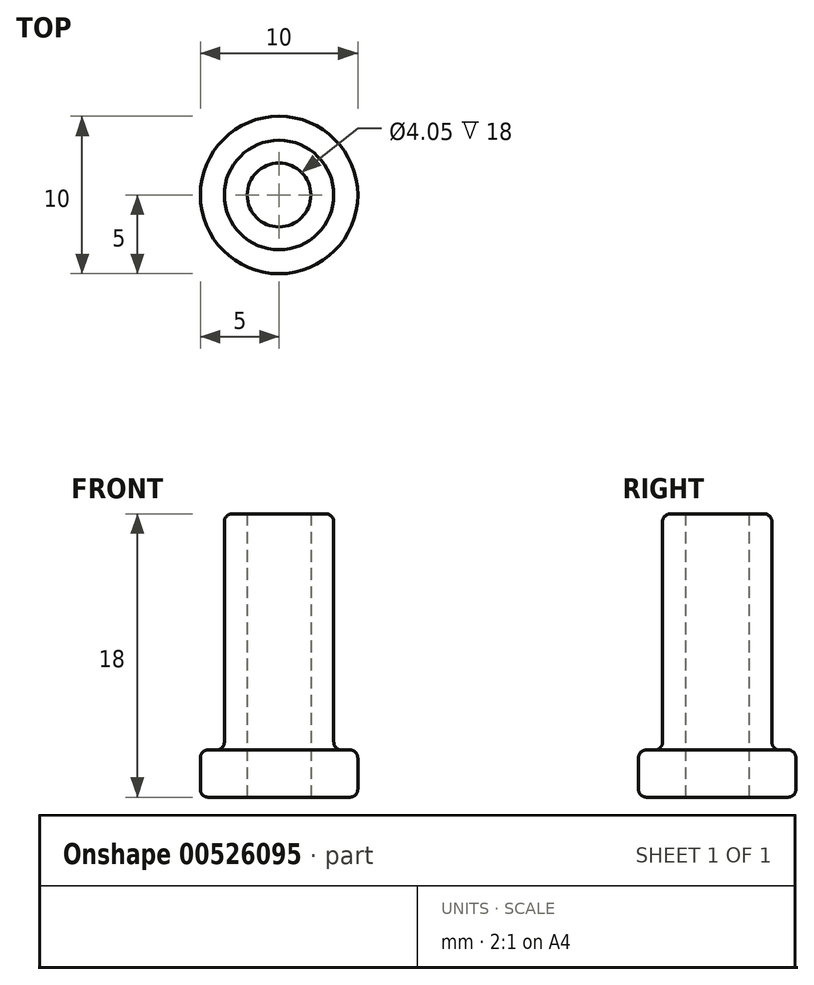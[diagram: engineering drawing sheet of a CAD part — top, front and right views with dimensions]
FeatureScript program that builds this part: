
annotation { "Feature Type Name" : "Feature", "Feature Type Description" : "" }
export const myFeature = defineFeature(function(context is Context, id is Id, definition is map)
    precondition{}
    {
        {
            var Q0;
            Q0=qCreatedBy(makeId("Front.planeOp"),FACE);
            var sketch = newSketch(context, id + "F0", { "sketchPlane" : qUnion([Q0])});
            skLineSegment(sketch, "E0", {"start": v(0, 0) * mm, "end": v(0, 40) * mm});
            skLineSegment(sketch, "E1", {"start": v(2.02, 0) * mm, "end": v(5, 0) * mm});
            skLineSegment(sketch, "E2.0", {"start": v(2.02, 18) * mm, "end": v(3.47, 18) * mm});
            skLineSegment(sketch, "E3.0", {"start": v(3.47, 3) * mm, "end": v(5, 3) * mm});
            skLineSegment(sketch, "E4.0", {"start": v(5, 0) * mm, "end": v(5, 3) * mm});
            skPoint(sketch, "E5.orphan", {"position": v(-20.83, 0) * mm});
            skLineSegment(sketch, "E6.0", {"start": v(2.02, 0) * mm, "end": v(2.02, 18) * mm});
            skLineSegment(sketch, "E7", {"start": v(3.47, 18) * mm, "end": v(3.47, 3) * mm});
            skSolve(sketch);
        }
        {
            var Q0;
            Q0=makeQuery(id+"F0.imprint","IMPRINT",FACE,{"disambiguationData":[TD([[makeQuery(id+"F0.imprint","IMPRINT",EDGE,{"derivedFrom":sQuery(id+"F0.wireOp",EDGE,"E2.0")}),-1.0]])]});
            var Q1;
            Q1=sQuery(id+"F0.wireOp",EDGE,"E0");
            revolve(context, id + "F1", {"entities" : qUnion([Q0]), "axis" : qUnion([Q1]), "revolveType" : RevolveType.FULL});
        }
        {
            var Q0;
            Q0=makeQuery(id+"F1.opRevolve","SWEPT_FACE",FACE,{"disambiguationData":[OSD([sQuery(id+"F0.wireOp",EDGE,"E7")])]});
            var Q1;
            Q1=makeQuery(id+"F1.opRevolve","SWEPT_FACE",FACE,{"disambiguationData":[OSD([sQuery(id+"F0.wireOp",EDGE,"E4.0")])]});
            var Q2;
            Q2=makeQuery(id+"F1.opRevolve","SWEPT_EDGE",EDGE,{"disambiguationData":[OSD([sQuery(id+"F0.wireOp",EDGE,"E3.0"),sQuery(id+"F0.wireOp",EDGE,"E4.0")])]});
            var Q3;
            Q3=makeQuery(id+"F1.opRevolve","SWEPT_EDGE",EDGE,{"disambiguationData":[OSD([sQuery(id+"F0.wireOp",EDGE,"E3.0"),sQuery(id+"F0.wireOp",EDGE,"E7")])]});
            fillet(context, id + "F2", {"entities" : qUnion([Q0, Q1, Q2, Q3]), "radius" : 0.5 * mm, "tangentPropagation" : true, "allowEdgeOverflow" : false});
        }
    });
